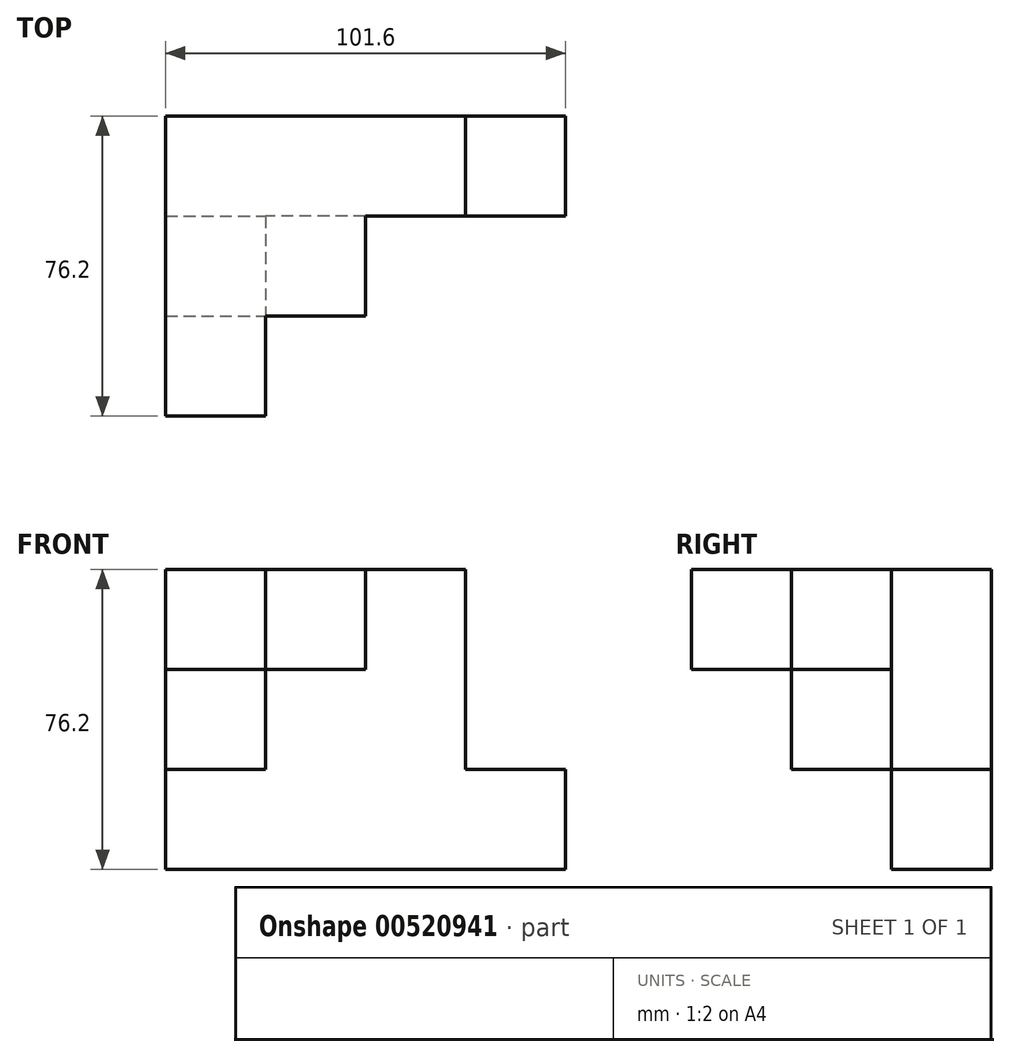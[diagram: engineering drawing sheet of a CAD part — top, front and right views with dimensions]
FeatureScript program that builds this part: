
annotation { "Feature Type Name" : "Feature", "Feature Type Description" : "" }
export const myFeature = defineFeature(function(context is Context, id is Id, definition is map)
    precondition{}
    {
        {
            var Q0;
            Q0=qCreatedBy(makeId("Front.planeOp"),FACE);
            var sketch = newSketch(context, id + "F0", { "sketchPlane" : qUnion([Q0])});
            skLineSegment(sketch, "E0.bottom", {"start": v(0, 0) * mm, "end": v(101.6, 0) * mm});
            skLineSegment(sketch, "E0.top", {"start": v(0, 76.2) * mm, "end": v(101.6, 76.2) * mm});
            skLineSegment(sketch, "E0.left", {"start": v(0, 0) * mm, "end": v(0, 76.2) * mm});
            skLineSegment(sketch, "E0.right", {"start": v(101.6, 0) * mm, "end": v(101.6, 76.2) * mm});
            skSolve(sketch);
        }
        {
            var Q0;
            Q0=makeQuery(id+"F0.imprint","IMPRINT",FACE,{"disambiguationData":[TD([[makeQuery(id+"F0.imprint","IMPRINT",EDGE,{"derivedFrom":sQuery(id+"F0.wireOp",EDGE,"E0.bottom")}),1.0]])]});
            extrude(context, id + "F1", {"entities" : qUnion([Q0]), "depth" : 25.4 * mm, "offsetDistance" : 25.4 * mm});
        }
        {
            var Q0;
            Q0=makeQuery(id+"F1.opExtrude","CAP_FACE",FACE,{"disambiguationData":[OSD([sQuery(id+"F0.wireOp",EDGE,"E0.bottom"),sQuery(id+"F0.wireOp",EDGE,"E0.top"),sQuery(id+"F0.wireOp",EDGE,"E0.left"),sQuery(id+"F0.wireOp",EDGE,"E0.right")])],"isStart":false});
            var sketch = newSketch(context, id + "F2", { "sketchPlane" : qUnion([Q0])});
            skLineSegment(sketch, "E1.bottom", {"start": v(101.6, 76.2) * mm, "end": v(76.2, 76.2) * mm});
            skLineSegment(sketch, "E1.top", {"start": v(101.6, 25.4) * mm, "end": v(76.2, 25.4) * mm});
            skLineSegment(sketch, "E1.left", {"start": v(101.6, 76.2) * mm, "end": v(101.6, 25.4) * mm});
            skLineSegment(sketch, "E1.right", {"start": v(76.2, 76.2) * mm, "end": v(76.2, 25.4) * mm});
            skSolve(sketch);
        }
        {
            var Q0;
            Q0=makeQuery(id+"F2.imprint","IMPRINT",FACE,{"disambiguationData":[TD([[makeQuery(id+"F2.imprint","IMPRINT",EDGE,{"derivedFrom":sQuery(id+"F2.wireOp",EDGE,"E1.bottom")}),-1.0]])]});
            extrude(context, id + "F3", {"entities" : qUnion([Q0]), "operationType" : NewBodyOperationType.REMOVE, "oppositeDirection" : true, "depth" : 25.4 * mm, "offsetDistance" : 25.4 * mm});
        }
        {
            var Q0;
            Q0=makeQuery(id+"F1.opExtrude","CAP_FACE",FACE,{"disambiguationData":[OSD([sQuery(id+"F0.wireOp",EDGE,"E0.bottom"),sQuery(id+"F0.wireOp",EDGE,"E0.top"),sQuery(id+"F0.wireOp",EDGE,"E0.left"),sQuery(id+"F0.wireOp",EDGE,"E0.right")])],"isStart":false});
            var sketch = newSketch(context, id + "F4", { "sketchPlane" : qUnion([Q0])});
            skLineSegment(sketch, "E2.bottom", {"start": v(0, 76.2) * mm, "end": v(50.8, 76.2) * mm});
            skLineSegment(sketch, "E2.top", {"start": v(0, 25.4) * mm, "end": v(50.8, 25.4) * mm});
            skLineSegment(sketch, "E2.left", {"start": v(0, 76.2) * mm, "end": v(0, 25.4) * mm});
            skLineSegment(sketch, "E2.right", {"start": v(50.8, 76.2) * mm, "end": v(50.8, 25.4) * mm});
            skSolve(sketch);
        }
        {
            var Q0;
            Q0=makeQuery(id+"F4.imprint","IMPRINT",FACE,{"disambiguationData":[TD([[makeQuery(id+"F4.imprint","IMPRINT",EDGE,{"derivedFrom":sQuery(id+"F4.wireOp",EDGE,"E2.bottom")}),-1.0]])]});
            extrude(context, id + "F5", {"entities" : qUnion([Q0]), "operationType" : NewBodyOperationType.ADD, "depth" : 25.4 * mm, "offsetDistance" : 25.4 * mm});
        }
        {
            var Q0;
            Q0=makeQuery(id+"F5.opExtrude","CAP_FACE",FACE,{"disambiguationData":[OSD([sQuery(id+"F4.wireOp",EDGE,"E2.bottom"),sQuery(id+"F4.wireOp",EDGE,"E2.top"),sQuery(id+"F4.wireOp",EDGE,"E2.left"),sQuery(id+"F4.wireOp",EDGE,"E2.right")])],"isStart":false});
            var sketch = newSketch(context, id + "F6", { "sketchPlane" : qUnion([Q0])});
            skLineSegment(sketch, "E3.bottom", {"start": v(50.8, 25.4) * mm, "end": v(25.4, 25.4) * mm});
            skLineSegment(sketch, "E3.top", {"start": v(50.8, 50.8) * mm, "end": v(25.4, 50.8) * mm});
            skLineSegment(sketch, "E3.left", {"start": v(50.8, 25.4) * mm, "end": v(50.8, 50.8) * mm});
            skLineSegment(sketch, "E3.right", {"start": v(25.4, 25.4) * mm, "end": v(25.4, 50.8) * mm});
            skSolve(sketch);
        }
        {
            var Q0;
            Q0=makeQuery(id+"F6.imprint","IMPRINT",FACE,{"disambiguationData":[TD([[makeQuery(id+"F6.imprint","IMPRINT",EDGE,{"derivedFrom":sQuery(id+"F6.wireOp",EDGE,"E3.bottom")}),1.0]])]});
            extrude(context, id + "F7", {"entities" : qUnion([Q0]), "operationType" : NewBodyOperationType.REMOVE, "oppositeDirection" : true, "depth" : 25.4 * mm, "offsetDistance" : 25.4 * mm});
        }
        {
            var Q0;
            Q0=makeQuery(id+"F5.opExtrude","CAP_FACE",FACE,{"disambiguationData":[OSD([sQuery(id+"F4.wireOp",EDGE,"E2.bottom"),sQuery(id+"F4.wireOp",EDGE,"E2.top"),sQuery(id+"F4.wireOp",EDGE,"E2.left"),sQuery(id+"F4.wireOp",EDGE,"E2.right")])],"isStart":false});
            var sketch = newSketch(context, id + "F8", { "sketchPlane" : qUnion([Q0])});
            skLineSegment(sketch, "E4.bottom", {"start": v(0, 76.2) * mm, "end": v(25.4, 76.2) * mm});
            skLineSegment(sketch, "E4.top", {"start": v(0, 50.8) * mm, "end": v(25.4, 50.8) * mm});
            skLineSegment(sketch, "E4.left", {"start": v(0, 76.2) * mm, "end": v(0, 50.8) * mm});
            skLineSegment(sketch, "E4.right", {"start": v(25.4, 76.2) * mm, "end": v(25.4, 50.8) * mm});
            skSolve(sketch);
        }
        {
            var Q0;
            Q0=makeQuery(id+"F8.imprint","IMPRINT",FACE,{"disambiguationData":[TD([[makeQuery(id+"F8.imprint","IMPRINT",EDGE,{"derivedFrom":sQuery(id+"F8.wireOp",EDGE,"E4.bottom")}),-1.0]])]});
            extrude(context, id + "F9", {"entities" : qUnion([Q0]), "operationType" : NewBodyOperationType.ADD, "depth" : 25.4 * mm, "offsetDistance" : 25.4 * mm});
        }
    });
